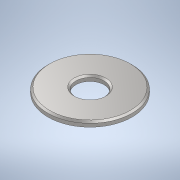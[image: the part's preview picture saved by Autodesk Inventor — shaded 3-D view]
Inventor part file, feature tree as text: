
AUTODESK INVENTOR PART (.ipt)
format: ipt  version: 2021 (Build 250183000, 183)  size: 110,080 bytes
history: native  units: mm
features: extrude x1, chamfer x1, sketch x1
ambient origin geometry x8: Origin, YZ Plane, XZ Plane, XY Plane, X Axis, Y Axis, Z Axis, Center Point
bodies: Solid1 (feature_tree)
feature tree (3):
  extrude  "Extrusion1"  Depth=1.5mm
  chamfer  "Chamfer1"  Distance=1.5mm
  sketch  "Sketch1"  dims[d0=8.4mm d1=25.0mm d2=1.5mm d3=0.0mm d4=0.5mm d5=2.0mm d6=45.0deg]
